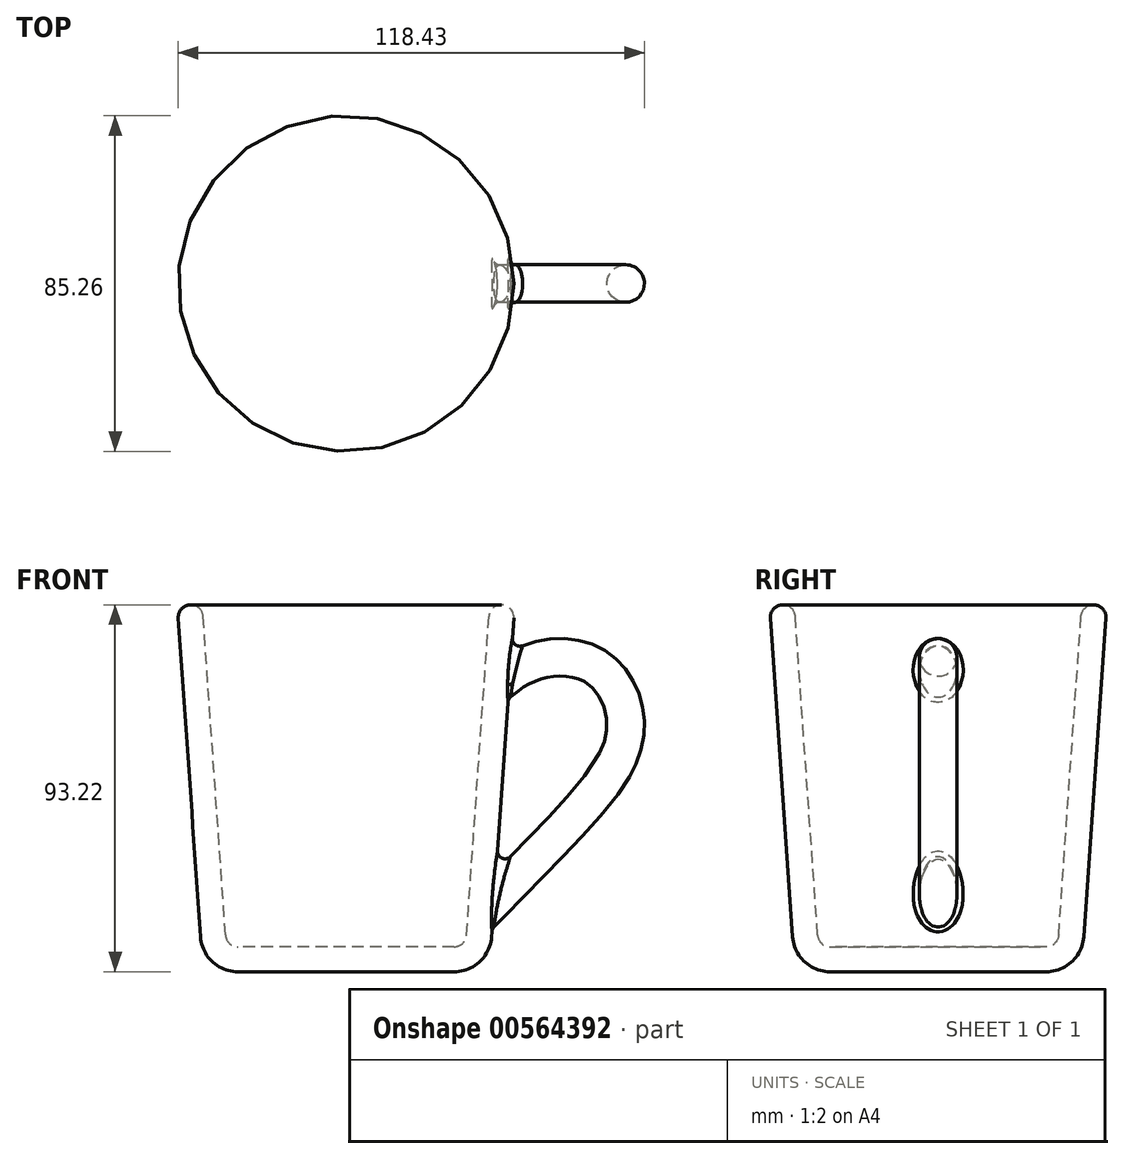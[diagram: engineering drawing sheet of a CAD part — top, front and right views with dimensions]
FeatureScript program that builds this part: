
annotation { "Feature Type Name" : "Feature", "Feature Type Description" : "" }
export const myFeature = defineFeature(function(context is Context, id is Id, definition is map)
    precondition{}
    {
        {
            var Q0;
            Q0=qCreatedBy(makeId("Top.planeOp"),FACE);
            var sketch = newSketch(context, id + "F0", { "sketchPlane" : qUnion([Q0])});
            skCircle(sketch, "E0", {"center": v(0, 0) * mm, "radius": 42.86 * mm});
            skSolve(sketch);
        }
        {
            var Q0;
            Q0=makeQuery(id+"F0.imprint","IMPRINT",FACE,{"disambiguationData":[TD([[makeQuery(id+"F0.imprint","IMPRINT",EDGE,{"derivedFrom":sQuery(id+"F0.wireOp",EDGE,"E0")}),1.0]])]});
            var Q1;
            Q1=sQuery(id+"F0.wireOp",EDGE,"E0");
            extrude(context, id + "F1", {"entities" : qUnion([Q0]), "surfaceEntities" : qUnion([Q1]), "oppositeDirection" : true, "depth" : 93.22 * mm, "offsetDistance" : 25.4 * mm, "hasDraft" : true, "draftAngle" : 4 * degree, "draftPullDirection" : true});
        }
        {
            var Q0;
            Q0=makeQuery(id+"F1.opExtrude","CAP_EDGE",EDGE,{"disambiguationData":[OSD([sQuery(id+"F0.wireOp",EDGE,"E0")])],"isStart":false});
            fillet(context, id + "F2", {"entities" : qUnion([Q0]), "radius" : 9.52 * mm, "tangentPropagation" : true, "allowEdgeOverflow" : false});
        }
        {
            var Q0;
            Q0=makeQuery(id+"F1.opExtrude","CAP_FACE",FACE,{"disambiguationData":[OSD([sQuery(id+"F0.wireOp",EDGE,"E0")])],"isStart":true});
            shell(context, id + "F3", {"entities" : qUnion([Q0]), "thickness" : 6.35 * mm});
        }
        {
            var Q0;
            Q0=makeQuery(id+"F1.opExtrude","CAP_EDGE",EDGE,{"disambiguationData":[OSD([sQuery(id+"F0.wireOp",EDGE,"E0")])],"isStart":true});
            var Q1;
            {var subQ0=sQuery(id+"F0.wireOp",EDGE,"E0");Q1=makeQuery(id+"F3.opShell","OFFSET_EDGE",EDGE,{"disambiguationData":[OSD([subQ0]),TDD([makeQuery(id+"F1.opExtrude","CAP_EDGE",EDGE,{"disambiguationData":[OSD([subQ0])],"isStart":true})])]});}
            fillet(context, id + "F4", {"entities" : qUnion([Q0, Q1]), "radius" : 3.17 * mm, "tangentPropagation" : true, "allowEdgeOverflow" : false});
        }
        {
            var Q0;
            Q0=qCreatedBy(makeId("Front.planeOp"),FACE);
            var sketch = newSketch(context, id + "F5", { "sketchPlane" : qUnion([Q0])});
            skFitSpline(sketch, "E1", {"points": [v(40.8, -18.15) * mm, v(63.06, -15.48) * mm, v(71.02, -31.4) * mm, v(36.83, -75.83) * mm], "startDerivative": vector(69.43, 55.9) * mm, "endDerivative": vector(-157.69, -161.9) * mm});
            skLineSegment(sketch, "E2", {"start": v(0, 0) * mm, "end": v(0, -94.47) * mm, "construction": true});
            skSolve(sketch);
        }
        {
            var Q0;
            Q0=sQuery(id+"F5.wireOp",EDGE,"E1");
            var Q1;
            Q1=sQuery(id+"F5.wireOp",VERTEX,"E1.start");
            cPlane(context, id + "F6", {"entities" : qUnion([Q0, Q1]), "cplaneType" : CPlaneType.CURVE_POINT, "offset" : 25.4 * mm, "width" : 152.4 * mm, "height" : 152.4 * mm});
        }
        {
            var Q0;
            Q0=qCreatedBy(id+"F6.planeOp",FACE);
            var sketch = newSketch(context, id + "F7", { "sketchPlane" : qUnion([Q0])});
            skCircle(sketch, "E3", {"center": v(0, -39.73) * mm, "radius": 4.76 * mm});
            skSolve(sketch);
        }
        {
            var Q0;
            Q0=makeQuery(id+"F7.imprint","IMPRINT",FACE,{"disambiguationData":[TD([[makeQuery(id+"F7.imprint","IMPRINT",EDGE,{"derivedFrom":sQuery(id+"F7.wireOp",EDGE,"E3")}),1.0]])]});
            var Q1;
            Q1=sQuery(id+"F5.wireOp",EDGE,"E1");
            sweep(context, id + "F8", {"operationType" : NewBodyOperationType.ADD, "profiles" : qUnion([Q0]), "path" : qUnion([Q1])});
        }
        {
            var Q0;
            Q0=makeQuery(id+"F8.opSweep","CAP_FACE",FACE,{"disambiguationData":[OSD([sQuery(id+"F5.wireOp",VERTEX,"E1.start"),sQuery(id+"F7.wireOp",EDGE,"E3")])],"isStart":true});
            var Q1;
            Q1=makeQuery(id+"F1.opExtrude","SWEPT_FACE",FACE,{"disambiguationData":[OSD([sQuery(id+"F0.wireOp",EDGE,"E0")])]});
            extrude(context, id + "F9", {"entities" : qUnion([Q0]), "operationType" : NewBodyOperationType.ADD, "endBound" : BoundingType.UP_TO_SURFACE, "depth" : 25.4 * mm, "endBoundEntityFace" : qUnion([Q1]), "offsetDistance" : 25.4 * mm});
        }
        {
            var Q0;
            Q0=makeQuery(id+"F8.opSweep","CAP_FACE",FACE,{"disambiguationData":[OSD([sQuery(id+"F5.wireOp",VERTEX,"E1.end"),sQuery(id+"F7.wireOp",EDGE,"E3")])],"isStart":false});
            var Q1;
            Q1=makeQuery(id+"F1.opExtrude","SWEPT_FACE",FACE,{"disambiguationData":[OSD([sQuery(id+"F0.wireOp",EDGE,"E0")])]});
            extrude(context, id + "F10", {"entities" : qUnion([Q0]), "operationType" : NewBodyOperationType.ADD, "endBound" : BoundingType.UP_TO_SURFACE, "depth" : 25.4 * mm, "endBoundEntityFace" : qUnion([Q1]), "offsetDistance" : 25.4 * mm});
        }
        {
            var Q0;
            Q0=makeQuery(id+"F10.opExtrude","CAP_EDGE",EDGE,{"disambiguationData":[OSD([sQuery(id+"F5.wireOp",VERTEX,"E1.end"),sQuery(id+"F7.wireOp",EDGE,"E3")])],"isStart":false});
            var Q1;
            Q1=makeQuery(id+"F8.boolean.opBoolean","INTERSECT",EDGE,{"disambiguationData":[OD(0.0)],"derivedFrom":[makeQuery(id+"F1.opExtrude","SWEPT_FACE",FACE,{"disambiguationData":[OSD([sQuery(id+"F0.wireOp",EDGE,"E0")])]}),makeQuery(id+"F8.opSweep","SWEPT_FACE",FACE,{"disambiguationData":[OSD([sQuery(id+"F5.wireOp",EDGE,"E1"),sQuery(id+"F7.wireOp",EDGE,"E3")])]})]});
            fillet(context, id + "F11", {"entities" : qUnion([Q0, Q1]), "radius" : 1.9 * mm, "tangentPropagation" : true, "allowEdgeOverflow" : false});
        }
    });
